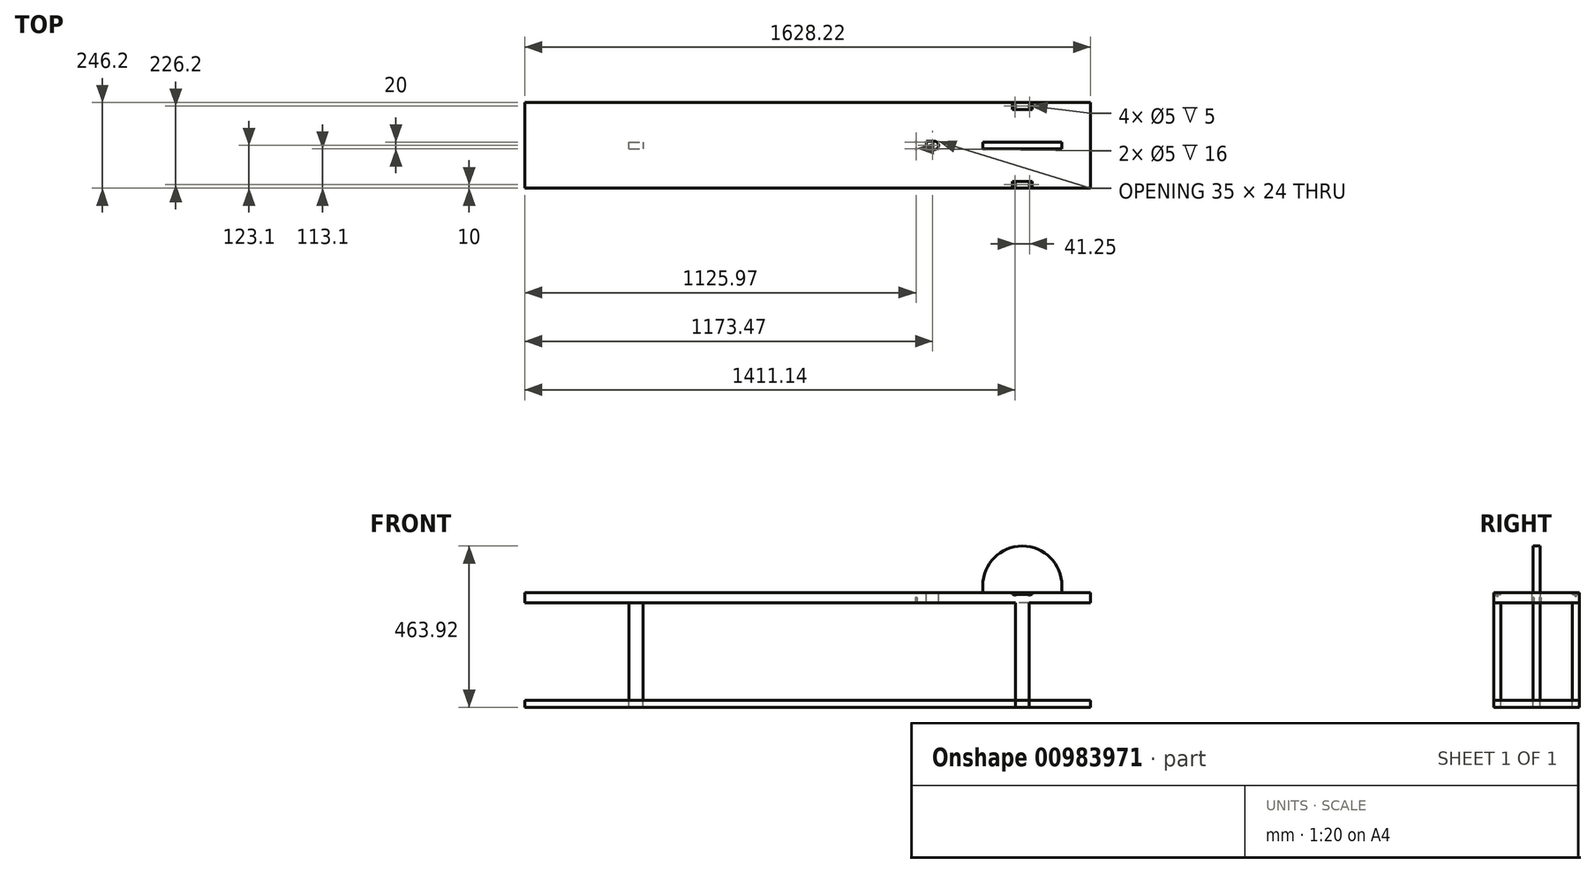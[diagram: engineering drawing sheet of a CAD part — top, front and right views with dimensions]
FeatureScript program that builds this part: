
annotation { "Feature Type Name" : "Feature", "Feature Type Description" : "" }
export const myFeature = defineFeature(function(context is Context, id is Id, definition is map)
    precondition{}
    {
        {
            var Q0;
            Q0=qCreatedBy(makeId("Top.planeOp"),FACE);
            var sketch = newSketch(context, id + "F0", { "sketchPlane" : qUnion([Q0])});
            skLineSegment(sketch, "E0", {"start": v(0, 0) * mm, "end": v(0, -123.1) * mm});
            skLineSegment(sketch, "E1", {"start": v(0, -123.1) * mm, "end": v(-1628.22, -123.1) * mm});
            skLineSegment(sketch, "E2", {"start": v(0, 0) * mm, "end": v(0, 123.1) * mm});
            skLineSegment(sketch, "E3", {"start": v(0, 123.1) * mm, "end": v(-1628.22, 123.1) * mm});
            skLineSegment(sketch, "E4", {"start": v(-1628.22, -123.1) * mm, "end": v(-1628.22, 123.1) * mm});
            skSolve(sketch);
        }
        {
            var Q0;
            Q0 = qSketchRegion(id + "F0", true);
            extrude(context, id + "F1", {"entities" : qUnion([Q0]), "oppositeDirection" : true, "depth" : 30 * mm, "offsetDistance" : 25 * mm});
        }
        {
            var Q0;
            Q0=qCreatedBy(makeId("Front.planeOp"),FACE);
            var sketch = newSketch(context, id + "F2", { "sketchPlane" : qUnion([Q0])});
            skLineSegment(sketch, "E5", {"start": v(-82.53, 0) * mm, "end": v(-196.45, 0) * mm});
            skArc(sketch, "E6", {"start": v(-82.53, 20) * mm, "mid": v(-196.45, 133.92) * mm, "end": v(-310.37, 20) * mm});
            skLineSegment(sketch, "E7", {"start": v(-82.53, 20) * mm, "end": v(-82.53, 0) * mm});
            skLineSegment(sketch, "E8", {"start": v(-310.37, 20) * mm, "end": v(-310.37, 0) * mm});
            skLineSegment(sketch, "E9", {"start": v(-196.45, 0) * mm, "end": v(-310.37, 0) * mm});
            skSolve(sketch);
        }
        {
            var Q0;
            Q0=makeQuery(id+"F2.imprint","IMPRINT",FACE,{"disambiguationData":[TD([[makeQuery(id+"F2.imprint","IMPRINT",EDGE,{"derivedFrom":sQuery(id+"F2.wireOp",EDGE,"E5")}),-1.0]])]});
            extrude(context, id + "F3", {"entities" : qUnion([Q0]), "depth" : 10 * mm, "offsetDistance" : 25 * mm, "hasSecondDirection" : true, "secondDirectionOppositeDirection" : true, "secondDirectionDepth" : 10 * mm});
        }
        {
            var Q0;
            Q0=qCreatedBy(makeId("Top.planeOp"),FACE);
            var sketch = newSketch(context, id + "F4", { "sketchPlane" : qUnion([Q0])});
            skLineSegment(sketch, "E10", {"start": v(-460.75, 12) * mm, "end": v(-449.25, 12) * mm});
            skLineSegment(sketch, "E11", {"start": v(-449.25, -12) * mm, "end": v(-472.25, -12) * mm});
            skLineSegment(sketch, "E12", {"start": v(-472.25, -12) * mm, "end": v(-472.25, 12) * mm});
            skLineSegment(sketch, "E13", {"start": v(-472.25, 12) * mm, "end": v(-460.75, 12) * mm});
            skArc(sketch, "E14", {"start": v(-449.25, -12) * mm, "mid": v(-437.25, 0) * mm, "end": v(-449.25, 12) * mm});
            skPoint(sketch, "E15.start.orphan", {"position": v(-472.25, 0) * mm});
            skSolve(sketch);
        }
        {
            var Q0;
            Q0=makeQuery(id+"F4.imprint","IMPRINT",FACE,{"disambiguationData":[TD([[makeQuery(id+"F4.imprint","IMPRINT",EDGE,{"derivedFrom":sQuery(id+"F4.wireOp",EDGE,"E10")}),-1.0]])]});
            extrude(context, id + "F5", {"entities" : qUnion([Q0]), "operationType" : NewBodyOperationType.REMOVE, "endBound" : BoundingType.THROUGH_ALL, "oppositeDirection" : true, "depth" : 25 * mm, "offsetDistance" : 25 * mm});
        }
        {
            var Q0;
            Q0=qCreatedBy(makeId("Top.planeOp"),FACE);
            var sketch = newSketch(context, id + "F6", { "sketchPlane" : qUnion([Q0])});
            skLineSegment(sketch, "E16", {"start": v(0, 0) * mm, "end": v(-196.45, 0) * mm});
            skLineSegment(sketch, "E17", {"start": v(-196.45, 123.1) * mm, "end": v(-167.32, 123.1) * mm});
            skLineSegment(sketch, "E18", {"start": v(-167.32, 123.1) * mm, "end": v(-167.32, 103.1) * mm});
            skLineSegment(sketch, "E19", {"start": v(-167.32, 103.1) * mm, "end": v(-225.57, 103.1) * mm});
            skLineSegment(sketch, "E20", {"start": v(-225.57, 103.1) * mm, "end": v(-225.57, 123.1) * mm});
            skLineSegment(sketch, "E21", {"start": v(-225.57, 123.1) * mm, "end": v(-196.45, 123.1) * mm});
            skCircle(sketch, "E22", {"center": v(-217.07, 113.1) * mm, "radius": 2.5 * mm});
            skCircle(sketch, "E23", {"center": v(-175.82, 113.1) * mm, "radius": 2.5 * mm});
            skPoint(sketch, "E24.orphan", {"position": v(-225.57, 113.1) * mm});
            skLineSegment(sketch, "E25.MirrorCS", {"start": v(-167.32, -103.1) * mm, "end": v(-225.57, -103.1) * mm});
            skLineSegment(sketch, "E26.MirrorCS", {"start": v(-167.32, -123.1) * mm, "end": v(-167.32, -103.1) * mm});
            skLineSegment(sketch, "E27.MirrorCS", {"start": v(-225.57, -103.1) * mm, "end": v(-225.57, -123.1) * mm});
            skLineSegment(sketch, "E28.MirrorCS", {"start": v(-225.57, -123.1) * mm, "end": v(-196.45, -123.1) * mm});
            skLineSegment(sketch, "E29.MirrorCS", {"start": v(-196.45, -123.1) * mm, "end": v(-167.32, -123.1) * mm});
            skCircle(sketch, "E30.MirrorC", {"center": v(-175.82, -113.1) * mm, "radius": 2.5 * mm});
            skCircle(sketch, "E31.MirrorC", {"center": v(-217.07, -113.1) * mm, "radius": 2.5 * mm});
            skSolve(sketch);
        }
        {
            var Q0;
            Q0=makeQuery(id+"F6.imprint","IMPRINT",FACE,{"disambiguationData":[TD([[makeQuery(id+"F6.imprint","IMPRINT",EDGE,{"derivedFrom":sQuery(id+"F6.wireOp",EDGE,"E17")}),-1.0]])]});
            var Q1;
            Q1=makeQuery(id+"F6.imprint","IMPRINT",FACE,{"disambiguationData":[TD([[makeQuery(id+"F6.imprint","IMPRINT",EDGE,{"derivedFrom":sQuery(id+"F6.wireOp",EDGE,"E25.MirrorCS")}),1.0]])]});
            extrude(context, id + "F7", {"entities" : qUnion([Q0, Q1]), "operationType" : NewBodyOperationType.REMOVE, "oppositeDirection" : true, "depth" : 5 * mm, "offsetDistance" : 25 * mm});
        }
        {
            var Q0;
            Q0=makeQuery(id+"F7.boolean.opBoolean","SPLIT",FACE,{"disambiguationData":[TD([makeQuery(id+"F7.opExtrude","SWEPT_FACE",FACE,{"disambiguationData":[OSD([sQuery(id+"F6.wireOp",EDGE,"E23")])]})])],"derivedFrom":makeQuery(id+"F1.opExtrude","CAP_FACE",FACE,{"disambiguationData":[OSD([sQuery(id+"F0.wireOp",EDGE,"E0"),sQuery(id+"F0.wireOp",EDGE,"E1"),sQuery(id+"F0.wireOp",EDGE,"E2"),sQuery(id+"F0.wireOp",EDGE,"E3"),sQuery(id+"F0.wireOp",EDGE,"E4")])],"isStart":true})});
            var Q1;
            Q1=makeQuery(id+"F7.boolean.opBoolean","SPLIT",FACE,{"disambiguationData":[TD([makeQuery(id+"F7.opExtrude","SWEPT_FACE",FACE,{"disambiguationData":[OSD([sQuery(id+"F6.wireOp",EDGE,"E22")])]})])],"derivedFrom":makeQuery(id+"F1.opExtrude","CAP_FACE",FACE,{"disambiguationData":[OSD([sQuery(id+"F0.wireOp",EDGE,"E0"),sQuery(id+"F0.wireOp",EDGE,"E1"),sQuery(id+"F0.wireOp",EDGE,"E2"),sQuery(id+"F0.wireOp",EDGE,"E3"),sQuery(id+"F0.wireOp",EDGE,"E4")])],"isStart":true})});
            var Q2;
            Q2=makeQuery(id+"F7.boolean.opBoolean","SPLIT",FACE,{"disambiguationData":[TD([makeQuery(id+"F7.opExtrude","SWEPT_FACE",FACE,{"disambiguationData":[OSD([sQuery(id+"F6.wireOp",EDGE,"E30.MirrorC")])]})])],"derivedFrom":makeQuery(id+"F1.opExtrude","CAP_FACE",FACE,{"disambiguationData":[OSD([sQuery(id+"F0.wireOp",EDGE,"E0"),sQuery(id+"F0.wireOp",EDGE,"E1"),sQuery(id+"F0.wireOp",EDGE,"E2"),sQuery(id+"F0.wireOp",EDGE,"E3"),sQuery(id+"F0.wireOp",EDGE,"E4")])],"isStart":true})});
            var Q3;
            Q3=makeQuery(id+"F7.boolean.opBoolean","SPLIT",FACE,{"disambiguationData":[TD([makeQuery(id+"F7.opExtrude","SWEPT_FACE",FACE,{"disambiguationData":[OSD([sQuery(id+"F6.wireOp",EDGE,"E31.MirrorC")])]})])],"derivedFrom":makeQuery(id+"F1.opExtrude","CAP_FACE",FACE,{"disambiguationData":[OSD([sQuery(id+"F0.wireOp",EDGE,"E0"),sQuery(id+"F0.wireOp",EDGE,"E1"),sQuery(id+"F0.wireOp",EDGE,"E2"),sQuery(id+"F0.wireOp",EDGE,"E3"),sQuery(id+"F0.wireOp",EDGE,"E4")])],"isStart":true})});
            extrude(context, id + "F8", {"entities" : qUnion([Q0, Q1, Q2, Q3]), "operationType" : NewBodyOperationType.REMOVE, "oppositeDirection" : true, "depth" : 10 * mm, "offsetDistance" : 25 * mm});
        }
        {
            var Q0;
            {var subQ0=sQuery(id+"F0.wireOp",EDGE,"E2");var subQ1=sQuery(id+"F0.wireOp",EDGE,"E0");var subQ2=sQuery(id+"F0.wireOp",EDGE,"E1");var subQ3=sQuery(id+"F0.wireOp",EDGE,"E3");var subQ4=sQuery(id+"F0.wireOp",EDGE,"E4");Q0=makeQuery(id+"F7.boolean.opBoolean","SPLIT",FACE,{"disambiguationData":[TD([makeQuery(id+"F1.opExtrude","SWEPT_FACE",FACE,{"disambiguationData":[OSD([subQ2])]})])],"derivedFrom":makeQuery(id+"F1.opExtrude","CAP_FACE",FACE,{"disambiguationData":[OSD([subQ1,subQ2,subQ0,subQ3,subQ4])],"isStart":true})});}
            cPlane(context, id + "F9", {"entities" : qUnion([Q0]), "cplaneType" : CPlaneType.OFFSET, "offset" : 30 * mm, "oppositeDirection" : true, "width" : 150 * mm, "height" : 150 * mm});
        }
        {
            var Q0;
            Q0=qCreatedBy(id+"F9.planeOp",FACE);
            var sketch = newSketch(context, id + "F10", { "sketchPlane" : qUnion([Q0])});
            skCircle(sketch, "E32", {"center": v(-502.25, -10) * mm, "radius": 2.5 * mm});
            skCircle(sketch, "E33", {"center": v(-502.25, 10) * mm, "radius": 2.5 * mm});
            skSolve(sketch);
        }
        {
            var Q0;
            Q0=makeQuery(id+"F10.imprint","IMPRINT",FACE,{"disambiguationData":[TD([[makeQuery(id+"F10.imprint","IMPRINT",EDGE,{"derivedFrom":sQuery(id+"F10.wireOp",EDGE,"E32")}),1.0]])]});
            var Q1;
            Q1=makeQuery(id+"F10.imprint","IMPRINT",FACE,{"disambiguationData":[TD([[makeQuery(id+"F10.imprint","IMPRINT",EDGE,{"derivedFrom":sQuery(id+"F10.wireOp",EDGE,"E33")}),1.0]])]});
            extrude(context, id + "F11", {"entities" : qUnion([Q0, Q1]), "operationType" : NewBodyOperationType.REMOVE, "depth" : 16 * mm, "offsetDistance" : 25 * mm});
        }
        {
            var Q0;
            Q0=qCreatedBy(id+"F9.planeOp",FACE);
            var sketch = newSketch(context, id + "F12", { "sketchPlane" : qUnion([Q0])});
            skLineSegment(sketch, "E34", {"start": v(0, 0) * mm, "end": v(-196.45, 0) * mm});
            skLineSegment(sketch, "E35", {"start": v(-196.45, -123.1) * mm, "end": v(-176.45, -123.1) * mm});
            skLineSegment(sketch, "E36", {"start": v(-176.45, -123.1) * mm, "end": v(-176.45, -103.1) * mm});
            skLineSegment(sketch, "E37", {"start": v(-176.45, -103.1) * mm, "end": v(-216.45, -103.1) * mm});
            skLineSegment(sketch, "E38", {"start": v(-216.45, -103.1) * mm, "end": v(-216.45, -123.1) * mm});
            skLineSegment(sketch, "E39", {"start": v(-216.45, -123.1) * mm, "end": v(-196.45, -123.1) * mm});
            skLineSegment(sketch, "E40.MirrorCS", {"start": v(-176.45, 103.1) * mm, "end": v(-216.45, 103.1) * mm});
            skLineSegment(sketch, "E41.MirrorCS", {"start": v(-176.45, 123.1) * mm, "end": v(-176.45, 103.1) * mm});
            skLineSegment(sketch, "E42.MirrorCS", {"start": v(-196.45, 123.1) * mm, "end": v(-176.45, 123.1) * mm});
            skLineSegment(sketch, "E43.MirrorCS", {"start": v(-216.45, 123.1) * mm, "end": v(-196.45, 123.1) * mm});
            skLineSegment(sketch, "E44.MirrorCS", {"start": v(-216.45, 103.1) * mm, "end": v(-216.45, 123.1) * mm});
            skLineSegment(sketch, "E45", {"start": v(-196.45, 0) * mm, "end": v(-1328.2, 0) * mm});
            skLineSegment(sketch, "E46", {"start": v(-1328.2, 0) * mm, "end": v(-1328.2, -10) * mm});
            skLineSegment(sketch, "E47", {"start": v(-1328.2, -10) * mm, "end": v(-1288.2, -10) * mm});
            skLineSegment(sketch, "E48.MirrorCS", {"start": v(-1328.2, 10) * mm, "end": v(-1288.2, 10) * mm});
            skLineSegment(sketch, "E49.MirrorCS", {"start": v(-1328.2, 0) * mm, "end": v(-1328.2, 10) * mm});
            skLineSegment(sketch, "E50", {"start": v(-1288.2, 10) * mm, "end": v(-1288.2, -10) * mm});
            skSolve(sketch);
        }
        {
            var Q0;
            Q0=makeQuery(id+"F12.imprint","IMPRINT",FACE,{"disambiguationData":[TD([[makeQuery(id+"F12.imprint","IMPRINT",EDGE,{"derivedFrom":sQuery(id+"F12.wireOp",EDGE,"E35")}),1.0]])]});
            var Q1;
            Q1=makeQuery(id+"F12.imprint","IMPRINT",FACE,{"disambiguationData":[TD([[makeQuery(id+"F12.imprint","IMPRINT",EDGE,{"derivedFrom":sQuery(id+"F12.wireOp",EDGE,"E40.MirrorCS")}),-1.0]])]});
            var Q2;
            {var subQ4=sQuery(id+"F12.wireOp",EDGE,"E48.MirrorCS");Q2=makeQuery(id+"F12.imprint","IMPRINT",FACE,{"disambiguationData":[TD([[makeQuery(id+"F12.imprint","IMPRINT",EDGE,{"derivedFrom":subQ4}),-1.0]])]});}
            var Q3;
            {var subQ0=sQuery(id+"F12.wireOp",EDGE,"E46");Q3=makeQuery(id+"F12.imprint","IMPRINT",FACE,{"disambiguationData":[TD([[makeQuery(id+"F12.imprint","IMPRINT",EDGE,{"derivedFrom":subQ0}),1.0]])]});}
            extrude(context, id + "F13", {"entities" : qUnion([Q0, Q1, Q2, Q3]), "operationType" : NewBodyOperationType.ADD, "oppositeDirection" : true, "depth" : 300 * mm, "offsetDistance" : 25 * mm});
        }
        {
            var Q0;
            Q0=makeQuery(id+"F1.opExtrude","CAP_FACE",FACE,{"disambiguationData":[OSD([sQuery(id+"F0.wireOp",EDGE,"E0"),sQuery(id+"F0.wireOp",EDGE,"E1"),sQuery(id+"F0.wireOp",EDGE,"E2"),sQuery(id+"F0.wireOp",EDGE,"E3"),sQuery(id+"F0.wireOp",EDGE,"E4")])],"isStart":false});
            cPlane(context, id + "F14", {"entities" : qUnion([Q0]), "cplaneType" : CPlaneType.OFFSET, "offset" : 300 * mm, "width" : 150 * mm, "height" : 150 * mm});
        }
        {
            var Q0;
            Q0=qCreatedBy(id+"F14.planeOp",FACE);
            var sketch = newSketch(context, id + "F15", { "sketchPlane" : qUnion([Q0])});
            skLineSegment(sketch, "E51", {"start": v(0, 0) * mm, "end": v(0, 123.1) * mm});
            skLineSegment(sketch, "E52", {"start": v(0, 123.1) * mm, "end": v(-1628.22, 123.1) * mm});
            skLineSegment(sketch, "E53", {"start": v(0, 0) * mm, "end": v(0, -123.1) * mm});
            skLineSegment(sketch, "E54", {"start": v(0, -123.1) * mm, "end": v(-1628.22, -123.1) * mm});
            skLineSegment(sketch, "E55", {"start": v(-1628.22, -123.1) * mm, "end": v(-1628.22, 123.1) * mm});
            skSolve(sketch);
        }
        {
            var Q0;
            Q0=makeQuery(id+"F15.imprint","IMPRINT",FACE,{"disambiguationData":[TD([[makeQuery(id+"F15.imprint","IMPRINT",EDGE,{"derivedFrom":sQuery(id+"F15.wireOp",EDGE,"E51")}),1.0]])]});
            extrude(context, id + "F16", {"entities" : qUnion([Q0]), "oppositeDirection" : true, "depth" : 20 * mm, "offsetDistance" : 25 * mm});
        }
    });
